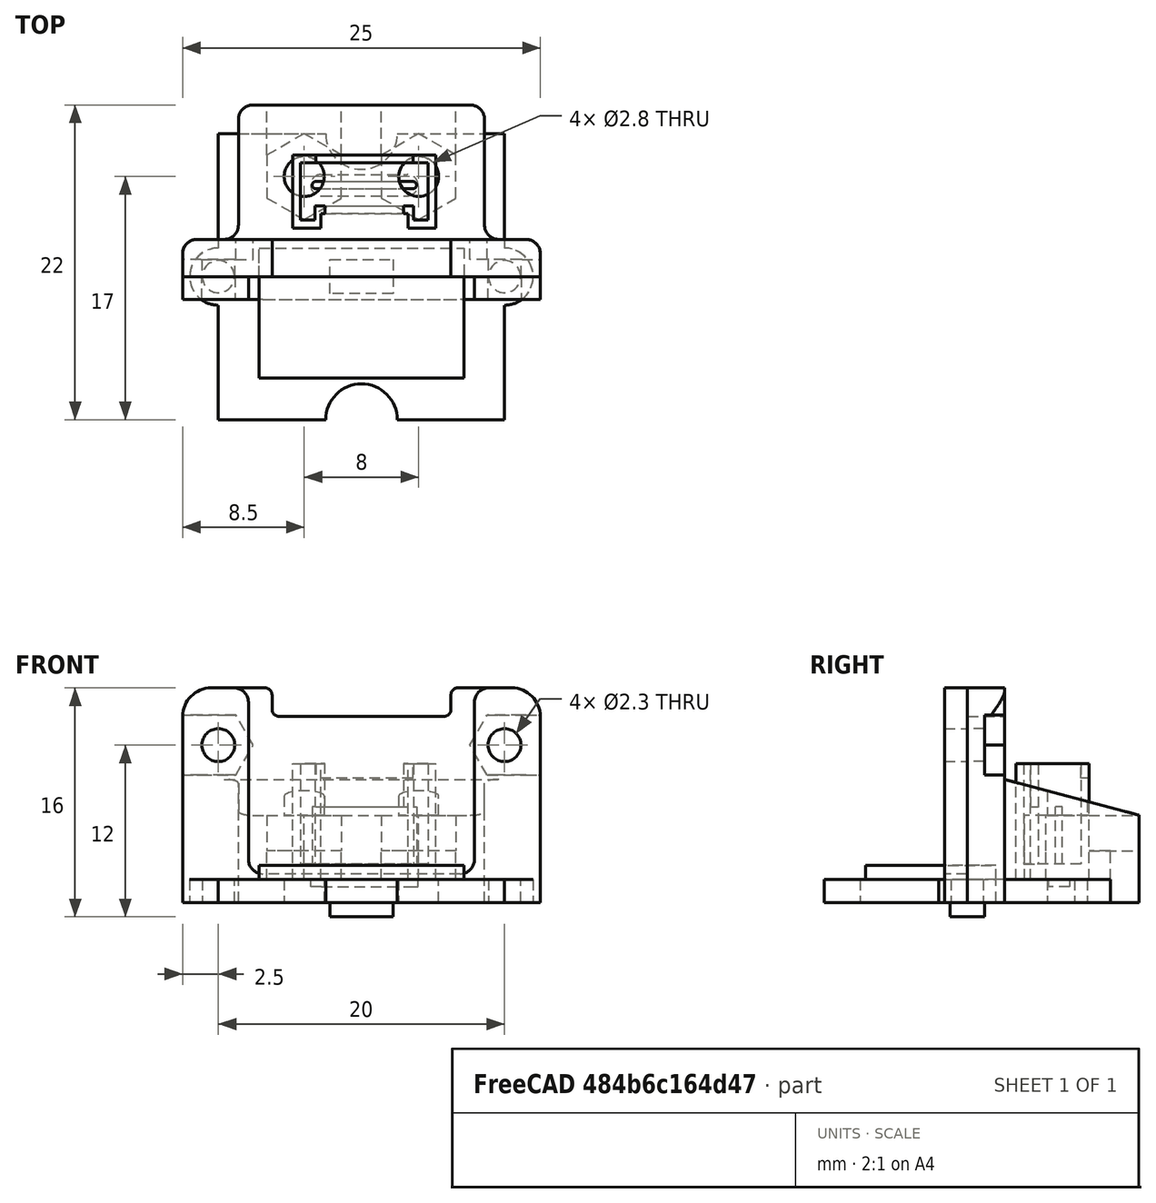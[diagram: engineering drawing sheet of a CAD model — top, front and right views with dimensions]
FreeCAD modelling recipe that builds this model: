
FCSTD DOCUMENT  (FreeCAD 0.19R24276 (Git))
Label: PB3D_TriPlate_LSRMt
License: All rights reserved
LicenseURL: http://en.wikipedia.org/wiki/All_rights_reserved
objects: Sketcher::SketchObject×23, PartDesign::Pocket×13, PartDesign::Pad×8, PartDesign::Body×6, PartDesign::Plane×3, App::Part×2, Mesh::Feature×2, Spreadsheet::Sheet×1
note: 74 computed .brp shape members not serialized (recipe doc carries the construction recipe); baked Part::Feature solids carry a one-line shape summary decoded from their .brp

FEATURE [Spreadsheet::Sheet] Spreadsheet  label="params"
  cells = A1=M2 Bolt Clearances; C1=M2.5 Bolt Clearances; A2=Hole Clear Diam; B2(m2_hole_clear_diam)==2.3mm; C2=Hole Clear Diam; D2(m25_hole_clear_diam)==2.8mm; E2=Std Rad; F2(std_rad)==2mm; A3=Head Clear Diam; B3(m2_head_clear_diam)==4mm; C3=Head Clear Diam; D3(m25_head_clear_diam)==5mm; A4=Head Min Depth; B4(m2_head_min_depth)==1.3mm; C4=Head Min Depth; D4(m25_head_min_depth)==1.6mm; A5=Nut Clear Flat; B5(m2_nut_clear_flat)==4.2mm; C5=Nut Clear Flat; D5(m25_nut_clear_flat)==5.2mm; A6=Nut Min Depth; B6(m2_nut_min_depth)==1.75mm; C6=Nut Min Depth; D6(m25_nut_min_depth)==2mm; A8=LSR Mt; G8=LSR Face Plate; A9=Mt Height; B9(mt_height)==15mm; C9=ToPlate CSunk Z; D9(toplate_csunk_z)==1.6mm; E9=Grove Con Clear Width; F9(grove_clear_width)==12.5mm; G9=Grove Plate Thick; H9(faceplate_grovethick)==1.5mm; A10=Mt Width; B10(mt_width)==25mm; C10=ToPlate CSunk Height; D10(toplate_csunk_height)==m25_nut_min_depth; E10=Grove Con Clear Height; F10(grove_clear_height)==2mm; G10=Grove+Elec thick; H10(faceplate_grovetotthick)==2.75mm; A11=Mt Thick; B11(mt_thick)==2.6mm; C11=ToPlate Slot Z; D11(toplate_slot_z)==toplate_csunk_z + toplate_csunk_height; G11=Face Plate Tol; H11(faceplate_tol)==0.35mm; A12=Foot Width; B12(foot_width)==12mm; C12=ToPlate Slot Height; D12(toplate_slot_height)==m25_nut_min_depth + 0.5mm; G12=Face Plate Thick; H12(faceplate_thick)==faceplate_grovetotthick - faceplate_grovethick + faceplate_tol; A13=Foot Thick; B13(foot_thick)==toplate_slot_z + toplate_slot_height; G13=Face Plate Cut Width; H13(faceplate_cut_width)==15.8mm; C14=ToPlate Hole Spacing Y; D14(toplate_hole_spacing_x)==8mm; G14=Face Plate Bottom Height; H14(faceplate_bottom_height)==2mm; A15=LSR Mt CSunk Offset Z; B15(lsr_mt_csunk_z)==1.2mm; C15=ToPlate Hole Offset X; D15(toplate_hole_offset_y)==5mm; A16=LSR Mt Hole Spacing Width; B16(lsr_mt_hole_spacing_width)==20mm; C16=ToPlate Hole Loc X; D16(toplate_hole_loc_y)==foot_width - toplate_hole_offset_y; A17=LSR Mt Hole Height; B17(lsr_mt_hole_height)==11mm; A19=Sculpt Z Width; B19(sculpt_z_width)==17.2mm
FEATURE [Sketcher::SketchObject] Sketch008
  FullyConstrained = true
  MapMode = 5
  Support = -> [XY_Plane007]
  sketch-geometry (8):
    g0: LineSegment StartX=-5 StartY=0 StartZ=0 EndX=-3.05 EndY=0 EndZ=0
    g1: LineSegment StartX=3.05 StartY=0 StartZ=0 EndX=5 EndY=0 EndZ=0
    g2: LineSegment StartX=-5 StartY=0 StartZ=0 EndX=-5 EndY=5.1 EndZ=0
    g3: LineSegment StartX=-5 StartY=5.1 StartZ=0 EndX=5 EndY=5.1 EndZ=0
    g4: LineSegment StartX=5 StartY=5.1 StartZ=0 EndX=5 EndY=0 EndZ=0
    g5: LineSegment StartX=3.05 StartY=0 StartZ=0 EndX=3.05 EndY=1 EndZ=0
    g6: LineSegment StartX=3.05 StartY=1 StartZ=0 EndX=-3.05 EndY=1 EndZ=0
    g7: LineSegment StartX=-3.05 StartY=1 StartZ=0 EndX=-3.05 EndY=0 EndZ=0
  constraints (23):
    c: PointOnObject(g0,g-1)
    c: PointOnObject(g1,g-1)
    c: PointOnObject(g0,g-1)
    c: Coincident(g2,g0)
    c: Vertical(g2)
    c: Coincident(g3,g2)
    c: Horizontal(g3)
    c: Coincident(g4,g3)
    c: Coincident(g4,g1)
    c: Vertical(g4)
    c: Coincident(g5,g1)
    c: Vertical(g5)
    c: Coincident(g6,g5)
    c: Horizontal(g6)
    c: Coincident(g7,g6)
    c: Coincident(g7,g0)
    c: Vertical(g7)
    c: Equal(g0,g1)
    c: Symmetric(g0,g1,g-1)
    c: Distance(g4) = 5.1
    c: Distance(g6) = 6.1
    c: Distance(g3) = 10
    c: Distance(g7) = 1
FEATURE [PartDesign::Pad] Pad005
  Direction = (1,1,1)
  Length = 8.1
  Length2 = 100
  Profile = -> Sketch008
  Type = 0
FEATURE [Sketcher::SketchObject] Sketch013
  FullyConstrained = true
  MapMode = 5
  Support = -> [XY_Plane007]
  sketch-geometry (5):
    g0: ArcOfCircle CenterX=-3 CenterY=3 CenterZ=0 NormalX=0 NormalY=0 NormalZ=1 AngleXU=0 Radius=0.75 StartAngle=1.5708 EndAngle=4.71239
    g1: ArcOfCircle CenterX=3 CenterY=3 CenterZ=0 NormalX=0 NormalY=0 NormalZ=1 AngleXU=0 Radius=0.75 StartAngle=4.71239 EndAngle=7.85398
    g2: LineSegment StartX=-3 StartY=2.25 StartZ=0 EndX=3 EndY=2.25 EndZ=0
    g3: LineSegment StartX=-3 StartY=3.75 StartZ=0 EndX=3 EndY=3.75 EndZ=0
    g4: LineSegment StartX=0 StartY=0 StartZ=0 EndX=0 EndY=3 EndZ=0
  constraints (12):
    c: Tangent(g0,g3) = 1.5708
    c: Tangent(g0,g2) = -1.5708
    c: Tangent(g2,g1) = -1.5708
    c: Tangent(g3,g1) = 1.5708
    c: Horizontal(g2)
    c: Equal(g0,g1)
    c: Coincident(g4,g-1)
    c: PointOnObject(g4,g-2)
    c: Symmetric(g0,g1,g4)
    c: Distance(g4) = 3
    c: DistanceY(g1,g1) = 1.5
    c: DistanceX(g0,g1) = 6
FEATURE [Sketcher::SketchObject] Sketch009
  FullyConstrained = true
  MapMode = 5
  Placement = pos=(0,0,8.1) rot=(0,0,1;0rad)
  Support = -> [Pad005]
  sketch-geometry (10):
    g0: LineSegment StartX=-4.45 StartY=0.55 StartZ=0 EndX=-3.45 EndY=0.55 EndZ=0
    g1: LineSegment StartX=-3.45 StartY=0.55 StartZ=0 EndX=-3.45 EndY=1.55 EndZ=0
    g2: LineSegment StartX=-3.45 StartY=1.55 StartZ=0 EndX=3.45 EndY=1.55 EndZ=0
    g3: LineSegment StartX=3.45 StartY=1.55 StartZ=0 EndX=3.45 EndY=0.55 EndZ=0
    g4: LineSegment StartX=3.45 StartY=0.55 StartZ=0 EndX=4.45 EndY=0.55 EndZ=0
    g5: LineSegment StartX=4.45 StartY=0.55 StartZ=0 EndX=4.45 EndY=4.55 EndZ=0
    g6: LineSegment StartX=4.45 StartY=4.55 StartZ=0 EndX=-4.45 EndY=4.55 EndZ=0
    g7: LineSegment StartX=-4.45 StartY=4.55 StartZ=0 EndX=-4.45 EndY=0.55 EndZ=0
    g8: LineSegment StartX=-3.45 StartY=0.55 StartZ=0 EndX=3.45 EndY=0.55 EndZ=0
    g9: LineSegment StartX=0 StartY=0 StartZ=0 EndX=0 EndY=0.55 EndZ=0
  constraints (28):
    c: Horizontal(g0)
    c: Coincident(g1,g0)
    c: Coincident(g2,g1)
    c: Horizontal(g2)
    c: Coincident(g3,g2)
    c: Vertical(g3)
    c: Coincident(g4,g3)
    c: Horizontal(g4)
    c: Coincident(g5,g4)
    c: Vertical(g5)
    c: Coincident(g6,g5)
    c: Horizontal(g6)
    c: Coincident(g7,g6)
    c: Coincident(g7,g0)
    c: Vertical(g7)
    c: Vertical(g1)
    c: Coincident(g8,g0)
    c: Coincident(g8,g3)
    c: Horizontal(g8)
    c: Equal(g0,g4)
    c: Coincident(g9,g-1)
    c: PointOnObject(g9,g-2)
    c: Symmetric(g0,g3,g9)
    c: Distance(g0) = 1
    c: Distance(g1) = 1
    c: Distance(g9) = 0.55
    c: Distance(g6) = 8.9
    c: DistanceY(g2,g5) = 3
FEATURE [PartDesign::Pocket] Pocket003
  BaseFeature = -> Pad005
  Length = 7
  Length2 = 100
  Profile = -> Sketch009
  Type = 0
FEATURE [Sketcher::SketchObject] Sketch010
  FullyConstrained = true
  MapMode = 5
  Placement = pos=(0,0,8.1) rot=(0,0,1;0rad)
  Support = -> [Pocket003]
  sketch-geometry (5):
    g0: LineSegment StartX=0 StartY=0 StartZ=0 EndX=0 EndY=3 EndZ=0
    g1: LineSegment StartX=-3.4 StartY=8 StartZ=0 EndX=3.4 EndY=8 EndZ=0
    g2: LineSegment StartX=3.4 StartY=8 StartZ=0 EndX=3.4 EndY=3 EndZ=0
    g3: LineSegment StartX=3.4 StartY=3 StartZ=0 EndX=-3.4 EndY=3 EndZ=0
    g4: LineSegment StartX=-3.4 StartY=3 StartZ=0 EndX=-3.4 EndY=8 EndZ=0
  constraints (14):
    c: Coincident(g0,g-1)
    c: PointOnObject(g0,g-2)
    c: Coincident(g1,g2)
    c: Coincident(g2,g3)
    c: Coincident(g3,g4)
    c: Coincident(g4,g1)
    c: Horizontal(g1)
    c: Horizontal(g3)
    c: Vertical(g2)
    c: Vertical(g4)
    c: Symmetric(g3,g2,g0)
    c: Distance(g0) = 3
    c: Distance(g2) = 5
    c: Distance(g1) = 6.8
FEATURE [PartDesign::Pocket] Pocket004
  BaseFeature = -> Pocket003
  Length = 1
  Length2 = 100
  Profile = -> Sketch010
  Type = 0
FEATURE [Sketcher::SketchObject] Sketch011
  FullyConstrained = true
  MapMode = 5
  Placement = pos=(0,0,8.1) rot=(0,0,1;0rad)
  Support = -> [Pocket004]
  sketch-geometry (4):
    g0: LineSegment StartX=-2.75 StartY=3 StartZ=0 EndX=2.75 EndY=3 EndZ=0
    g1: LineSegment StartX=2.75 StartY=3 StartZ=0 EndX=2.75 EndY=0 EndZ=0
    g2: LineSegment StartX=2.75 StartY=0 StartZ=0 EndX=-2.75 EndY=0 EndZ=0
    g3: LineSegment StartX=-2.75 StartY=0 StartZ=0 EndX=-2.75 EndY=3 EndZ=0
  constraints (11):
    c: Coincident(g0,g1)
    c: Coincident(g1,g2)
    c: Coincident(g2,g3)
    c: Coincident(g3,g0)
    c: Horizontal(g0)
    c: Horizontal(g2)
    c: Vertical(g1)
    c: Vertical(g3)
    c: Symmetric(g2,g1,g-1)
    c: Distance(g1) = 3
    c: Distance(g0) = 5.5
FEATURE [PartDesign::Pocket] Pocket005
  BaseFeature = -> Pocket004
  Length = 3
  Length2 = 100
  Profile = -> Sketch011
  Type = 0
FEATURE [Sketcher::SketchObject] Sketch015
  FullyConstrained = true
  MapMode = 5
  Support = -> [XY_Plane010]
  sketch-geometry (4):
    g0: LineSegment StartX=-7.15 StartY=0 StartZ=0 EndX=7.15 EndY=0 EndZ=0
    g1: LineSegment StartX=7.15 StartY=0 StartZ=0 EndX=7.15 EndY=-9.1 EndZ=0
    g2: LineSegment StartX=7.15 StartY=-9.1 StartZ=0 EndX=-7.15 EndY=-9.1 EndZ=0
    g3: LineSegment StartX=-7.15 StartY=-9.1 StartZ=0 EndX=-7.15 EndY=0 EndZ=0
  constraints (11):
    c: Coincident(g0,g1)
    c: Coincident(g1,g2)
    c: Coincident(g2,g3)
    c: Coincident(g3,g0)
    c: Horizontal(g0)
    c: Horizontal(g2)
    c: Vertical(g1)
    c: Vertical(g3)
    c: Symmetric(g0,g0,g-1)
    c: Distance(g0) = 14.3
    c: Distance(g1) = 9.1
FEATURE [PartDesign::Pad] Pad009
  Direction = (1,1,1)
  Length = 1
  Length2 = 100
  Profile = -> Sketch015
  Type = 0
FEATURE [Sketcher::SketchObject] Sketch014
  FullyConstrained = true
  MapMode = 5
  Support = -> [XY_Plane010]
  sketch-geometry (6):
    g0: LineSegment StartX=-2.2 StartY=1.2 StartZ=0 EndX=2.2 EndY=1.2 EndZ=0
    g1: LineSegment StartX=2.2 StartY=1.2 StartZ=0 EndX=2.2 EndY=-1.2 EndZ=0
    g2: LineSegment StartX=2.2 StartY=-1.2 StartZ=0 EndX=-2.2 EndY=-1.2 EndZ=0
    g3: LineSegment StartX=-2.2 StartY=-1.2 StartZ=0 EndX=-2.2 EndY=1.2 EndZ=0
    g4: LineSegment StartX=0 StartY=0 StartZ=0 EndX=0 EndY=1.2 EndZ=0
    g5: LineSegment StartX=0 StartY=0 StartZ=0 EndX=2.2 EndY=0 EndZ=0
  constraints (16):
    c: Coincident(g0,g1)
    c: Coincident(g1,g2)
    c: Coincident(g2,g3)
    c: Coincident(g3,g0)
    c: Horizontal(g0)
    c: Horizontal(g2)
    c: Vertical(g1)
    c: Vertical(g3)
    c: Coincident(g4,g-1)
    c: PointOnObject(g4,g-2)
    c: Coincident(g5,g-1)
    c: PointOnObject(g5,g-1)
    c: Symmetric(g0,g0,g4)
    c: Symmetric(g0,g1,g5)
    c: Distance(g0) = 4.4
    c: Distance(g1) = 2.4
FEATURE [PartDesign::Pad] Pad008
  Direction = (1,1,1)
  Length = 1
  Length2 = 100
  Profile = -> Sketch014
  Reversed = true
  Type = 0
FEATURE [Sketcher::SketchObject] Sketch
  FullyConstrained = true
  MapMode = 5
  Support = -> [XY_Plane011]
  sketch-geometry (16):
    g0: LineSegment StartX=-10 StartY=10 StartZ=0 EndX=-2.5 EndY=10 EndZ=0
    g1: LineSegment StartX=2.5 StartY=10 StartZ=0 EndX=10 EndY=10 EndZ=0
    g2: LineSegment StartX=10 StartY=10 StartZ=0 EndX=10 EndY=2 EndZ=0
    g3: LineSegment StartX=10 StartY=-2 StartZ=0 EndX=10 EndY=-10 EndZ=0
    g4: LineSegment StartX=10 StartY=-10 StartZ=0 EndX=2.5 EndY=-10 EndZ=0
    g5: LineSegment StartX=-2.5 StartY=-10 StartZ=0 EndX=-10 EndY=-10 EndZ=0
    g6: LineSegment StartX=-10 StartY=-10 StartZ=0 EndX=-10 EndY=-2 EndZ=0
    g7: LineSegment StartX=-10 StartY=10 StartZ=0 EndX=-10 EndY=2 EndZ=0
    g8: ArcOfCircle CenterX=0 CenterY=10 CenterZ=0 NormalX=0 NormalY=0 NormalZ=1 AngleXU=0 Radius=2.5 StartAngle=3.14159 EndAngle=6.28319
    g9: ArcOfCircle CenterX=0 CenterY=-10 CenterZ=0 NormalX=0 NormalY=0 NormalZ=1 AngleXU=0 Radius=2.5 StartAngle=0 EndAngle=3.14159
    g10: LineSegment StartX=-2.5 StartY=10 StartZ=0 EndX=2.5 EndY=10 EndZ=0
    g11: LineSegment StartX=-2.5 StartY=-10 StartZ=0 EndX=2.5 EndY=-10 EndZ=0
    g12: LineSegment StartX=-10 StartY=2 StartZ=0 EndX=-10 EndY=-2 EndZ=0
    g13: LineSegment StartX=10 StartY=2 StartZ=0 EndX=10 EndY=-2 EndZ=0
    g14: ArcOfCircle CenterX=-10 CenterY=0 CenterZ=0 NormalX=0 NormalY=0 NormalZ=1 AngleXU=0 Radius=2 StartAngle=1.5708 EndAngle=4.71239
    g15: ArcOfCircle CenterX=10 CenterY=0 CenterZ=0 NormalX=0 NormalY=0 NormalZ=1 AngleXU=0 Radius=2 StartAngle=4.71239 EndAngle=7.85398
  constraints (48):
    c: Horizontal(g0)
    c: Horizontal(g1)
    c: Coincident(g2,g1)
    c: Vertical(g2)
    c: Vertical(g3)
    c: Coincident(g4,g3)
    c: Horizontal(g4)
    c: Horizontal(g5)
    c: Coincident(g6,g5)
    c: Vertical(g6)
    c: Coincident(g7,g0)
    c: Vertical(g7)
    c: PointOnObject(g8,g-2)
    c: Coincident(g8,g0)
    c: Coincident(g8,g1)
    c: PointOnObject(g9,g-2)
    c: Coincident(g9,g5)
    c: Coincident(g9,g4)
    c: Coincident(g10,g0)
    c: Coincident(g10,g1)
    c: Coincident(g11,g5)
    c: Coincident(g11,g4)
    c: Horizontal(g11)
    c: PointOnObject(g9,g11)
    c: PointOnObject(g8,g10)
    c: Horizontal(g10)
    c: Coincident(g12,g7)
    c: Coincident(g12,g6)
    c: Coincident(g13,g2)
    c: Coincident(g13,g3)
    c: Equal(g10,g11)
    c: Equal(g13,g12)
    c: Vertical(g12)
    c: Vertical(g13)
    c: PointOnObject(g14,g-1)
    c: Coincident(g14,g7)
    c: Coincident(g14,g6)
    c: PointOnObject(g15,g-1)
    c: Coincident(g15,g2)
    c: Coincident(g15,g3)
    c: PointOnObject(g14,g12)
    c: PointOnObject(g15,g13)
    c: Equal(g7,g6)
    c: Equal(g1,g0)
    c: Diameter(g14) = 4
    c: Diameter(g8) = 5
    c: DistanceY(g3,g1) = 20
    c: DistanceX(g0,g1) = 20
FEATURE [PartDesign::Pad] Pad
  Direction = (1,1,1)
  Length = 1.6
  Length2 = 100
  Profile = -> Sketch
  Type = 0
FEATURE [Sketcher::SketchObject] Sketch001
  FullyConstrained = true
  MapMode = 5
  Support = -> [XY_Plane011]
  sketch-geometry (2):
    g0: Circle CenterX=-10 CenterY=0 CenterZ=0 NormalX=0 NormalY=0 NormalZ=1 AngleXU=0 Radius=1.125
    g1: Circle CenterX=10 CenterY=0 CenterZ=0 NormalX=0 NormalY=0 NormalZ=1 AngleXU=0 Radius=1.125
  constraints (5):
    c: PointOnObject(g1,g-1)
    c: Symmetric(g0,g1,g-1)
    c: Equal(g0,g1)
    c: Diameter(g0) = 2.25
    c: DistanceX(g0,g1) = 20
FEATURE [PartDesign::Pocket] Pocket
  BaseFeature = -> Pad
  Length = 5
  Length2 = 100
  Profile = -> Sketch001
  Reversed = true
  Type = 1
FEATURE [Sketcher::SketchObject] Sketch012
  FullyConstrained = true
  MapMode = 5
  Placement = pos=(0,0,1.1) rot=(0,0,1;0rad)
  Support = -> [Pocket005]
  sketch-geometry (5):
    g0: ArcOfCircle CenterX=-3.4 CenterY=3 CenterZ=0 NormalX=0 NormalY=0 NormalZ=1 AngleXU=0 Radius=0.25 StartAngle=1.5708 EndAngle=4.71239
    g1: ArcOfCircle CenterX=3.4 CenterY=3 CenterZ=0 NormalX=0 NormalY=0 NormalZ=1 AngleXU=0 Radius=0.25 StartAngle=4.71239 EndAngle=7.85398
    g2: LineSegment StartX=-3.4 StartY=2.75 StartZ=0 EndX=3.4 EndY=2.75 EndZ=0
    g3: LineSegment StartX=-3.4 StartY=3.25 StartZ=0 EndX=3.4 EndY=3.25 EndZ=0
    g4: LineSegment StartX=0 StartY=0 StartZ=0 EndX=0 EndY=2.75 EndZ=0
  constraints (12):
    c: Tangent(g0,g3) = 1.5708
    c: Tangent(g0,g2) = -1.5708
    c: Tangent(g2,g1) = -1.5708
    c: Tangent(g3,g1) = 1.5708
    c: Horizontal(g2)
    c: Equal(g0,g1)
    c: Coincident(g4,g-1)
    c: PointOnObject(g4,g-2)
    c: Symmetric(g0,g1,g4)
    c: DistanceY(g-1,g1) = 3
    c: DistanceY(g1,g1) = 0.5
    c: DistanceX(g0,g1) = 6.8
FEATURE [PartDesign::Pad] Pad006
  BaseFeature = -> Pocket005
  Direction = (1,1,1)
  Length = 4
  Length2 = 100
  Profile = -> Sketch012
  Type = 0
FEATURE [PartDesign::Pad] Pad007
  BaseFeature = -> Pad006
  Direction = (1,1,1)
  Length = 0.5
  Length2 = 100
  Profile = -> Sketch013
  Reversed = true
  Type = 0
FEATURE [PartDesign::Body] Body001  label="GroveBoard"
  Group = -> [Sketch,Pad,Sketch001,Pocket]
  Origin = -> Origin003
  Tip = -> Pocket
FEATURE [PartDesign::Body] Body005  label="GroveHeader1"
  Group = -> [Sketch008,Pad005,Sketch009,Pocket003,Sketch010,Pocket004,Sketch011,Pocket005,Sketch012,Pad006,Sketch013,Pad007]
  Origin = -> Origin007
  Placement = pos=(0.2,3.4,1.6) rot=(0,0,1;0rad)
  Tip = -> Pad007
FEATURE [PartDesign::Body] Body006  label="LaserDistSens"
  Group = -> [Sketch014,Pad008]
  Origin = -> Origin008
  Tip = -> Pad008
FEATURE [PartDesign::Body] Body007  label="MiscElectronics"
  Group = -> [Sketch015,Pad009]
  Origin = -> Origin009
  Placement = pos=(0,2,1.6) rot=(0,0,1;0rad)
  Tip = -> Pad009
FEATURE [App::Part] Part001  label="Grove_LSR"
  Group = -> [Body001,Body005,Body006,Body007]
  Origin = -> Origin002
  Placement = pos=(-4e-16,-3,11) rot=(0,0.707107,0.707107;3.14159rad)
FEATURE [Sketcher::SketchObject] Sketch016  label="Sketch_MainMtExt"
  FullyConstrained = true
  MapMode = 5
  Placement = pos=(0,0,0) rot=(0.57735,0.57735,0.57735;2.0944rad)
  Support = -> [YZ_Plane001]
  expr: Constraints[11] = <<params>>.foot_thick
  expr: Constraints[8] = <<params>>.foot_width
  expr: Constraints[10] = <<params>>.mt_height
  expr: Constraints[9] = <<params>>.mt_thick
  sketch-geometry (6):
    g0: LineSegment StartX=0 StartY=0 StartZ=0 EndX=0 EndY=15 EndZ=0
    g1: LineSegment StartX=0 StartY=0 StartZ=0 EndX=12 EndY=0 EndZ=0
    g2: LineSegment StartX=0 StartY=15 StartZ=0 EndX=2.6 EndY=15 EndZ=0
    g3: LineSegment StartX=12 StartY=0 StartZ=0 EndX=12 EndY=6.1 EndZ=0
    g4: LineSegment StartX=2.6 StartY=15 StartZ=0 EndX=2.6 EndY=8.6 EndZ=0
    g5: LineSegment StartX=12 StartY=6.1 StartZ=0 EndX=2.6 EndY=8.6 EndZ=0
  constraints (17):
    c: Coincident(g0,g-1)
    c: PointOnObject(g0,g-2)
    c: Coincident(g1,g0)
    c: PointOnObject(g1,g-1)
    c: Coincident(g2,g0)
    c: Horizontal(g2)
    c: Coincident(g3,g1)
    c: Vertical(g3)
    c: DistanceX(g0,g1) = 12
    c: DistanceX(g0,g2) = 2.6
    c: DistanceY(g0,g0) = 15
    c: DistanceY(g1,g3) = 6.1
    c: Coincident(g4,g2)
    c: Vertical(g4)
    c: Coincident(g5,g3)
    c: Coincident(g5,g4)
    c: DistanceY(g3,g4) = 2.5
FEATURE [PartDesign::Pad] Pad010  label="MainExt"
  Direction = (1,1,1)
  Length = 25
  Length2 = 100
  Midplane = true
  Placement = pos=(0,0,0) rot=(0.57735,0.57735,0.57735;2.0944rad)
  Profile = -> Sketch016
  Type = 0
FEATURE [PartDesign::Plane] DatumPlane  label="Datum_ToPlateCSunkZ"
  AttachmentOffset = pos=(0,0,1.6) rot=(0,0,1;0rad)
  Length = 60
  MapMode = 5
  Placement = pos=(0,0,1.6) rot=(0,0,1;0rad)
  ResizeMode = 0
  Support = -> [XY_Plane001]
  Width = 60
  expr: .AttachmentOffset.Base.z = <<params>>.toplate_csunk_z
FEATURE [PartDesign::Plane] DatumPlane001  label="Datum_ToPlateSlotZ"
  AttachmentOffset = pos=(0,0,3.6) rot=(0,0,1;0rad)
  Length = 60
  MapMode = 5
  Placement = pos=(0,0,3.6) rot=(0,0,1;0rad)
  ResizeMode = 0
  Support = -> [XY_Plane001]
  Width = 60
  expr: .AttachmentOffset.Base.z = <<params>>.toplate_slot_z
FEATURE [Sketcher::SketchObject] Sketch017  label="Sketch_ToPlate_Temp"
  FullyConstrained = true
  MapMode = 5
  Support = -> [XY_Plane001]
  expr: Constraints[5] = Spreadsheet.toplate_hole_loc_y
  expr: Constraints[4] = Spreadsheet.toplate_hole_spacing_x
  sketch-geometry (2):
    g0: LineSegment StartX=0 StartY=0 StartZ=0 EndX=0 EndY=7 EndZ=0
    g1: LineSegment StartX=-4 StartY=7 StartZ=0 EndX=4 EndY=7 EndZ=0
  constraints (6):
    c: Coincident(g0,g-1)
    c: PointOnObject(g0,g-2)
    c: Horizontal(g1)
    c: Symmetric(g1,g1,g0)
    c: DistanceX(g1,g1) = 8
    c: DistanceY(g-1,g0) = 7
FEATURE [Sketcher::SketchObject] Sketch018  label="Sketch_ToPlate_Holes"
  FullyConstrained = true
  MapMode = 5
  Support = -> [XY_Plane001]
  expr: Constraints[9] = <<params>>.m25_hole_clear_diam
  expr: Constraints[4] = Spreadsheet.toplate_hole_spacing_x
  expr: Constraints[5] = Spreadsheet.toplate_hole_loc_y
  sketch-geometry (4):
    g0: LineSegment StartX=0 StartY=0 StartZ=0 EndX=0 EndY=7 EndZ=0
    g1: LineSegment StartX=-4 StartY=7 StartZ=0 EndX=4 EndY=7 EndZ=0
    g2: Circle CenterX=-4 CenterY=7 CenterZ=0 NormalX=0 NormalY=0 NormalZ=1 AngleXU=0 Radius=1.4
    g3: Circle CenterX=4 CenterY=7 CenterZ=0 NormalX=0 NormalY=0 NormalZ=1 AngleXU=0 Radius=1.4
  constraints (10):
    c: Coincident(g0,g-1)
    c: PointOnObject(g0,g-2)
    c: Horizontal(g1)
    c: Symmetric(g1,g1,g0)
    c: DistanceX(g1,g1) = 8
    c: DistanceY(g-1,g0) = 7
    c: Coincident(g2,g1)
    c: Coincident(g3,g1)
    c: Equal(g3,g2)
    c: Diameter(g3) = 2.8
FEATURE [PartDesign::Pocket] Pocket006  label="ToPlateMtHoles"
  BaseFeature = -> Pad010
  Length = 5
  Length2 = 100
  Placement = pos=(0,0,0) rot=(0.57735,0.57735,0.57735;2.0944rad)
  Profile = -> Sketch018
  Reversed = true
  Type = 1
FEATURE [Sketcher::SketchObject] Sketch019  label="Sketch_ToPlate_CSunk"
  FullyConstrained = true
  MapMode = 5
  Placement = pos=(0,0,1.6) rot=(0,0,1;0rad)
  Support = -> [DatumPlane]
  expr: Constraints[45] = <<params>>.m25_nut_clear_flat
  expr: Constraints[4] = Spreadsheet.toplate_hole_spacing_x
  expr: Constraints[5] = Spreadsheet.toplate_hole_loc_y
  sketch-geometry (16):
    g0: LineSegment StartX=0 StartY=0 StartZ=0 EndX=0 EndY=7 EndZ=0
    g1: LineSegment StartX=-4 StartY=7 StartZ=0 EndX=4 EndY=7 EndZ=0
    g2: LineSegment StartX=-4 StartY=10.0022 StartZ=0 EndX=-6.6 EndY=8.50111 EndZ=0
    g3: LineSegment StartX=-6.6 StartY=8.50111 StartZ=0 EndX=-6.6 EndY=5.49889 EndZ=0
    g4: LineSegment StartX=-6.6 StartY=5.49889 StartZ=0 EndX=-4 EndY=3.99778 EndZ=0
    g5: LineSegment StartX=-4 StartY=3.99778 StartZ=0 EndX=-1.4 EndY=5.49889 EndZ=0
    g6: LineSegment StartX=-1.4 StartY=5.49889 StartZ=0 EndX=-1.4 EndY=8.50111 EndZ=0
    g7: LineSegment StartX=-1.4 StartY=8.50111 StartZ=0 EndX=-4 EndY=10.0022 EndZ=0
    g8: Circle CenterX=-4 CenterY=7 CenterZ=0 NormalX=0 NormalY=0 NormalZ=1 AngleXU=0 Radius=3.00222
    g9: LineSegment StartX=4 StartY=10.0022 StartZ=0 EndX=1.4 EndY=8.50111 EndZ=0
    g10: LineSegment StartX=1.4 StartY=8.50111 StartZ=0 EndX=1.4 EndY=5.49889 EndZ=0
    g11: LineSegment StartX=1.4 StartY=5.49889 StartZ=0 EndX=4 EndY=3.99778 EndZ=0
    g12: LineSegment StartX=4 StartY=3.99778 StartZ=0 EndX=6.6 EndY=5.49889 EndZ=0
    g13: LineSegment StartX=6.6 StartY=5.49889 StartZ=0 EndX=6.6 EndY=8.50111 EndZ=0
    g14: LineSegment StartX=6.6 StartY=8.50111 StartZ=0 EndX=4 EndY=10.0022 EndZ=0
    g15: Circle CenterX=4 CenterY=7 CenterZ=0 NormalX=0 NormalY=0 NormalZ=1 AngleXU=0 Radius=3.00222
  constraints (38):
    c: Coincident(g0,g-1)
    c: PointOnObject(g0,g-2)
    c: Horizontal(g1)
    c: Symmetric(g1,g1,g0)
    c: DistanceX(g1,g1) = 8
    c: DistanceY(g-1,g0) = 7
    c: Coincident(g2,g3)
    c: Coincident(g3,g4)
    c: Coincident(g4,g5)
    c: Coincident(g5,g6)
    c: Coincident(g6,g7)
    c: Coincident(g7,g2)
    c: Equal(g2, g3-g7) x5
    c: PointOnObject(g2,g8)
    c: PointOnObject(g3,g8)
    c: PointOnObject(g4,g8)
    c: PointOnObject(g5,g8)
    c: PointOnObject(g6,g8)
    c: PointOnObject(g7,g8)
    c: Coincident(g8,g1)
    c: Coincident(g9,g10)
    c: Coincident(g10,g11)
    c: Coincident(g11,g12)
    c: Coincident(g12,g13)
    c: Coincident(g13,g14)
    c: Coincident(g14,g9)
    c: Equal(g9, g10-g14) x5
    c: PointOnObject(g9,g15)
    c: PointOnObject(g10,g15)
    c: PointOnObject(g11,g15)
    c: PointOnObject(g12,g15)
    c: PointOnObject(g13,g15)
    c: PointOnObject(g14,g15)
    c: Coincident(g15,g1)
    c: Vertical(g10)
    c: Vertical(g6)
    c: Equal(g8,g15)
    c: DistanceX(g10,g12) = 5.2
FEATURE [PartDesign::Pocket] Pocket007  label="ToPlateCSunk"
  BaseFeature = -> Pocket006
  Length = 2
  Length2 = 100
  Placement = pos=(0,0,0) rot=(0.57735,0.57735,0.57735;2.0944rad)
  Profile = -> Sketch019
  Reversed = true
  Type = 0
  expr: Length = <<params>>.m25_nut_min_depth
FEATURE [Sketcher::SketchObject] Sketch020  label="Sketch_ToPlate_Temp001"
  FullyConstrained = true
  MapMode = 5
  Placement = pos=(0,0,3.6) rot=(0,0,1;0rad)
  Support = -> [DatumPlane001]
  expr: Constraints[50] = <<params>>.foot_width
  expr: Constraints[35] = <<params>>.m25_nut_clear_flat
  expr: Constraints[4] = Spreadsheet.toplate_hole_spacing_x
  expr: Constraints[5] = Spreadsheet.toplate_hole_loc_y
  sketch-geometry (18):
    g0: LineSegment StartX=0 StartY=0 StartZ=0 EndX=0 EndY=7 EndZ=0
    g1: LineSegment StartX=-4 StartY=7 StartZ=0 EndX=4 EndY=7 EndZ=0
    g2: LineSegment StartX=-4 StartY=3.99778 StartZ=0 EndX=-1.4 EndY=5.49889 EndZ=0
    g3: LineSegment StartX=-1.4 StartY=5.49889 StartZ=0 EndX=-1.4 EndY=8.50111 EndZ=0
    g4: LineSegment StartX=-6.6 StartY=8.50111 StartZ=0 EndX=-6.6 EndY=5.49889 EndZ=0
    g5: LineSegment StartX=-6.6 StartY=5.49889 StartZ=0 EndX=-4 EndY=3.99778 EndZ=0
    g6: Circle CenterX=-4 CenterY=7 CenterZ=0 NormalX=0 NormalY=0 NormalZ=1 AngleXU=0 Radius=3.00222
    g7: LineSegment StartX=4 StartY=3.99778 StartZ=0 EndX=6.6 EndY=5.49889 EndZ=0
    g8: LineSegment StartX=6.6 StartY=5.49889 StartZ=0 EndX=6.6 EndY=8.50111 EndZ=0
    g9: LineSegment StartX=1.4 StartY=8.50111 StartZ=0 EndX=1.4 EndY=5.49889 EndZ=0
    g10: LineSegment StartX=1.4 StartY=5.49889 StartZ=0 EndX=4 EndY=3.99778 EndZ=0
    g11: Circle CenterX=4 CenterY=7 CenterZ=0 NormalX=0 NormalY=0 NormalZ=1 AngleXU=0 Radius=3.00222
    g12: LineSegment StartX=-6.6 StartY=8.50111 StartZ=0 EndX=-6.6 EndY=20.5011 EndZ=0
    g13: LineSegment StartX=-1.4 StartY=8.50111 StartZ=0 EndX=-1.4 EndY=20.5011 EndZ=0
    g14: LineSegment StartX=1.4 StartY=8.50111 StartZ=0 EndX=1.4 EndY=20.5011 EndZ=0
    g15: LineSegment StartX=6.6 StartY=8.50111 StartZ=0 EndX=6.6 EndY=20.5011 EndZ=0
    g16: LineSegment StartX=1.4 StartY=20.5011 StartZ=0 EndX=6.6 EndY=20.5011 EndZ=0
    g17: LineSegment StartX=-1.4 StartY=20.5011 StartZ=0 EndX=-6.6 EndY=20.5011 EndZ=0
  constraints (52):
    c: Coincident(g0,g-1)
    c: PointOnObject(g0,g-2)
    c: Horizontal(g1)
    c: Symmetric(g1,g1,g0)
    c: DistanceX(g1,g1) = 8
    c: DistanceY(g-1,g0) = 7
    c: Coincident(g2,g3)
    c: Coincident(g4,g5)
    c: Coincident(g5,g2)
    c: Equal(g2,g3)
    c: Equal(g2,g4)
    c: Equal(g2,g5)
    c: PointOnObject(g2,g6)
    c: PointOnObject(g3,g6)
    c: PointOnObject(g4,g6)
    c: PointOnObject(g4,g6)
    c: PointOnObject(g5,g6)
    c: Coincident(g6,g1)
    c: Coincident(g7,g8)
    c: Coincident(g9,g10)
    c: Coincident(g10,g7)
    c: Equal(g7,g8)
    c: Equal(g7,g9)
    c: Equal(g7,g10)
    c: PointOnObject(g7,g11)
    c: PointOnObject(g8,g11)
    c: PointOnObject(g9,g11)
    c: PointOnObject(g9,g11)
    c: PointOnObject(g10,g11)
    c: Coincident(g11,g1)
    c: Vertical(g4)
    c: Vertical(g8)
    c: Equal(g6,g11)
    c: Vertical(g3)
    c: Vertical(g9)
    c: DistanceX(g9,g7) = 5.2
    c: Coincident(g12,g4)
    c: Vertical(g12)
    c: Coincident(g13,g3)
    c: Vertical(g13)
    c: Coincident(g14,g9)
    c: Vertical(g14)
    c: Coincident(g15,g8)
    c: Vertical(g15)
    c: Coincident(g16,g14)
    c: Coincident(g16,g15)
    c: Horizontal(g16)
    c: Coincident(g17,g13)
    c: Coincident(g17,g12)
    c: Horizontal(g17)
    c: Distance(g15) = 12
    c: Equal(g14,g13)
FEATURE [PartDesign::Pocket] Pocket008  label="ToPlateSlot"
  BaseFeature = -> Pocket007
  Length = 2.5
  Length2 = 100
  Placement = pos=(0,0,0) rot=(0.57735,0.57735,0.57735;2.0944rad)
  Profile = -> Sketch020
  Reversed = true
  Type = 0
  expr: Length = <<params>>.toplate_slot_height
FEATURE [Sketcher::SketchObject] Sketch021  label="Sketch_SculptAlongZ"
  FullyConstrained = true
  MapMode = 5
  Support = -> [XY_Plane001]
  expr: Constraints[31] = <<params>>.sculpt_z_width
  expr: Constraints[30] = <<params>>.mt_width
  expr: Constraints[26] = <<params>>.mt_thick
  expr: Constraints[29] = <<params>>.foot_width
  sketch-geometry (18):
    g0: LineSegment StartX=-12.5 StartY=0 StartZ=0 EndX=-12.5 EndY=1.6 EndZ=0
    g1: LineSegment StartX=-11.5 StartY=2.6 StartZ=0 EndX=-9.6 EndY=2.6 EndZ=0
    g2: LineSegment StartX=-8.6 StartY=3.6 StartZ=0 EndX=-8.6 EndY=11 EndZ=0
    g3: LineSegment StartX=-7.6 StartY=12 StartZ=0 EndX=7.6 EndY=12 EndZ=0
    g4: LineSegment StartX=8.6 StartY=11 StartZ=0 EndX=8.6 EndY=3.6 EndZ=0
    g5: LineSegment StartX=9.6 StartY=2.6 StartZ=0 EndX=11.5 EndY=2.6 EndZ=0
    g6: LineSegment StartX=12.5 StartY=1.6 StartZ=0 EndX=12.5 EndY=0 EndZ=0
    g7: ArcOfCircle CenterX=-11.5 CenterY=1.6 CenterZ=0 NormalX=0 NormalY=0 NormalZ=1 AngleXU=0 Radius=1 StartAngle=1.5708 EndAngle=3.14159
    g8: ArcOfCircle CenterX=-9.6 CenterY=3.6 CenterZ=0 NormalX=0 NormalY=0 NormalZ=1 AngleXU=0 Radius=1 StartAngle=4.71239 EndAngle=6.28319
    g9: ArcOfCircle CenterX=-7.6 CenterY=11 CenterZ=0 NormalX=0 NormalY=0 NormalZ=1 AngleXU=0 Radius=1 StartAngle=1.5708 EndAngle=3.14159
    g10: ArcOfCircle CenterX=7.6 CenterY=11 CenterZ=0 NormalX=0 NormalY=0 NormalZ=1 AngleXU=0 Radius=1 StartAngle=0 EndAngle=1.5708
    g11: ArcOfCircle CenterX=9.6 CenterY=3.6 CenterZ=0 NormalX=0 NormalY=0 NormalZ=1 AngleXU=0 Radius=1 StartAngle=3.14159 EndAngle=4.71239
    g12: ArcOfCircle CenterX=11.5 CenterY=1.6 CenterZ=0 NormalX=0 NormalY=0 NormalZ=1 AngleXU=0 Radius=1 StartAngle=0 EndAngle=1.5708
    g13: LineSegment StartX=-12.5 StartY=0 StartZ=0 EndX=-22.5 EndY=0 EndZ=0
    g14: LineSegment StartX=12.5 StartY=0 StartZ=0 EndX=22.5 EndY=0 EndZ=0
    g15: LineSegment StartX=22.5 StartY=0 StartZ=0 EndX=22.5 EndY=22 EndZ=0
    g16: LineSegment StartX=22.5 StartY=22 StartZ=0 EndX=-22.5 EndY=22 EndZ=0
    g17: LineSegment StartX=-22.5 StartY=22 StartZ=0 EndX=-22.5 EndY=0 EndZ=0
  constraints (47):
    c: Symmetric(g0,g6,g-1)
    c: Vertical(g0)
    c: Horizontal(g1)
    c: Vertical(g2)
    c: Horizontal(g3)
    c: Vertical(g4)
    c: Horizontal(g5)
    c: Vertical(g6)
    c: Equal(g5,g1)
    c: Tangent(g0,g7) = 1.5708
    c: Tangent(g1,g7) = 1.5708
    c: Tangent(g1,g8) = -1.5708
    c: Tangent(g2,g8) = -1.5708
    c: Tangent(g2,g9) = 1.5708
    c: Tangent(g3,g9) = 1.5708
    c: Tangent(g3,g10) = 1.5708
    c: Tangent(g4,g10) = 1.5708
    c: Tangent(g4,g11) = -1.5708
    c: Tangent(g5,g11) = -1.5708
    c: Tangent(g5,g12) = 1.5708
    c: Tangent(g6,g12) = 1.5708
    c: Equal(g10,g9)
    c: Equal(g8,g11)
    c: Equal(g11,g12)
    c: Equal(g12,g7)
    c: Radius(g12) = 1
    c: DistanceY(g6,g5) = 2.6
    c: Equal(g6,g0)
    c: Equal(g10,g12)
    c: DistanceY(g-1,g3) = 12
    c: DistanceX(g0,g6) = 25
    c: DistanceX(g2,g4) = 17.2
    c: PointOnObject(g13,g-1)
    c: Horizontal(g13)
    c: Coincident(g14,g6)
    c: PointOnObject(g14,g-1)
    c: Coincident(g15,g14)
    c: Vertical(g15)
    c: Coincident(g16,g15)
    c: Horizontal(g16)
    c: Coincident(g17,g16)
    c: Coincident(g17,g13)
    c: Vertical(g17)
    c: DistanceY(g3,g15) = 10
    c: DistanceX(g6,g14) = 10
    c: Equal(g14,g13)
    c: Coincident(g0,g13)
FEATURE [PartDesign::Pocket] Pocket009  label="SculptAlongZ"
  BaseFeature = -> Pocket008
  Length = 5
  Length2 = 100
  Placement = pos=(0,0,0) rot=(0.57735,0.57735,0.57735;2.0944rad)
  Profile = -> Sketch021
  Reversed = true
  Type = 1
FEATURE [PartDesign::Plane] DatumPlane002  label="Datum_LSRMtCSunk"
  AttachmentOffset = pos=(0,0,-1.2) rot=(0,0,1;0rad)
  Length = 60
  MapMode = 5
  Placement = pos=(0,1.2,3e-16) rot=(1,0,0;1.5708rad)
  ResizeMode = 0
  Support = -> [XZ_Plane001]
  Width = 60
  expr: .AttachmentOffset.Base.z = -1 * <<params>>.lsr_mt_csunk_z
FEATURE [Sketcher::SketchObject] Sketch022  label="Sketch_LSRHoleMt_Temp"
  FullyConstrained = true
  MapMode = 5
  Placement = pos=(0,0,0) rot=(1,0,0;1.5708rad)
  Support = -> [XZ_Plane001]
  expr: Constraints[5] = <<params>>.lsr_mt_hole_spacing_width
  expr: Constraints[4] = <<params>>.lsr_mt_hole_height
  sketch-geometry (2):
    g0: LineSegment StartX=0 StartY=0 StartZ=0 EndX=0 EndY=11 EndZ=0
    g1: LineSegment StartX=-10 StartY=11 StartZ=0 EndX=10 EndY=11 EndZ=0
  constraints (6):
    c: Coincident(g0,g-1)
    c: PointOnObject(g0,g-2)
    c: Horizontal(g1)
    c: Symmetric(g1,g1,g0)
    c: DistanceY(g-1,g0) = 11
    c: DistanceX(g1,g1) = 20
FEATURE [Sketcher::SketchObject] Sketch023  label="Sketch_LSRMtHoles"
  FullyConstrained = true
  MapMode = 5
  Placement = pos=(0,0,0) rot=(1,0,0;1.5708rad)
  Support = -> [XZ_Plane001]
  expr: Constraints[9] = <<params>>.m2_hole_clear_diam
  expr: Constraints[4] = <<params>>.lsr_mt_hole_height
  expr: Constraints[5] = <<params>>.lsr_mt_hole_spacing_width
  sketch-geometry (4):
    g0: LineSegment StartX=0 StartY=0 StartZ=0 EndX=0 EndY=11 EndZ=0
    g1: LineSegment StartX=-10 StartY=11 StartZ=0 EndX=10 EndY=11 EndZ=0
    g2: Circle CenterX=-10 CenterY=11 CenterZ=0 NormalX=0 NormalY=0 NormalZ=1 AngleXU=0 Radius=1.15
    g3: Circle CenterX=10 CenterY=11 CenterZ=0 NormalX=0 NormalY=0 NormalZ=1 AngleXU=0 Radius=1.15
  constraints (10):
    c: Coincident(g0,g-1)
    c: PointOnObject(g0,g-2)
    c: Horizontal(g1)
    c: Symmetric(g1,g1,g0)
    c: DistanceY(g-1,g0) = 11
    c: DistanceX(g1,g1) = 20
    c: Coincident(g2,g1)
    c: Coincident(g3,g1)
    c: Equal(g3,g2)
    c: Diameter(g3) = 2.3
FEATURE [PartDesign::Pocket] Pocket010  label="LSRMtHoles"
  BaseFeature = -> Pocket009
  Length = 5
  Length2 = 100
  Placement = pos=(0,0,0) rot=(0.57735,0.57735,0.57735;2.0944rad)
  Profile = -> Sketch023
  Type = 1
FEATURE [Sketcher::SketchObject] Sketch024  label="Sketch_LSRCSunk"
  FullyConstrained = true
  MapMode = 5
  Placement = pos=(0,1.2,3e-16) rot=(1,0,0;1.5708rad)
  Support = -> [DatumPlane002]
  expr: Constraints[35] = <<params>>.m2_nut_clear_flat
  expr: Constraints[4] = <<params>>.lsr_mt_hole_height
  expr: Constraints[5] = <<params>>.lsr_mt_hole_spacing_width
  sketch-geometry (18):
    g0: LineSegment StartX=0 StartY=0 StartZ=0 EndX=0 EndY=11 EndZ=0
    g1: LineSegment StartX=-10 StartY=11 StartZ=0 EndX=10 EndY=11 EndZ=0
    g2: LineSegment StartX=7.57513 StartY=11 StartZ=0 EndX=8.78756 EndY=8.9 EndZ=0
    g3: LineSegment StartX=8.78756 StartY=8.9 StartZ=0 EndX=11.2124 EndY=8.9 EndZ=0
    g4: LineSegment StartX=11.2124 StartY=13.1 StartZ=0 EndX=8.78756 EndY=13.1 EndZ=0
    g5: LineSegment StartX=8.78756 StartY=13.1 StartZ=0 EndX=7.57513 EndY=11 EndZ=0
    g6: Circle CenterX=10 CenterY=11 CenterZ=0 NormalX=0 NormalY=0 NormalZ=1 AngleXU=0 Radius=2.42487
    g7: LineSegment StartX=-7.57513 StartY=11 StartZ=0 EndX=-8.78756 EndY=13.1 EndZ=0
    g8: LineSegment StartX=-8.78756 StartY=13.1 StartZ=0 EndX=-11.2124 EndY=13.1 EndZ=0
    g9: LineSegment StartX=-11.2124 StartY=8.9 StartZ=0 EndX=-8.78756 EndY=8.9 EndZ=0
    g10: LineSegment StartX=-8.78756 StartY=8.9 StartZ=0 EndX=-7.57513 EndY=11 EndZ=0
    g11: Circle CenterX=-10 CenterY=11 CenterZ=0 NormalX=0 NormalY=0 NormalZ=1 AngleXU=0 Radius=2.42487
    g12: LineSegment StartX=11.2124 StartY=13.1 StartZ=0 EndX=21.2124 EndY=13.1 EndZ=0
    g13: LineSegment StartX=11.2124 StartY=8.9 StartZ=0 EndX=21.2124 EndY=8.9 EndZ=0
    g14: LineSegment StartX=21.2124 StartY=8.9 StartZ=0 EndX=21.2124 EndY=13.1 EndZ=0
    g15: LineSegment StartX=-11.2124 StartY=8.9 StartZ=0 EndX=-21.2124 EndY=8.9 EndZ=0
    g16: LineSegment StartX=-11.2124 StartY=13.1 StartZ=0 EndX=-21.2124 EndY=13.1 EndZ=0
    g17: LineSegment StartX=-21.2124 StartY=8.9 StartZ=0 EndX=-21.2124 EndY=13.1 EndZ=0
  constraints (52):
    c: Coincident(g0,g-1)
    c: PointOnObject(g0,g-2)
    c: Horizontal(g1)
    c: Symmetric(g1,g1,g0)
    c: DistanceY(g-1,g0) = 11
    c: DistanceX(g1,g1) = 20
    c: Coincident(g2,g3)
    c: Coincident(g4,g5)
    c: Coincident(g5,g2)
    c: Equal(g2,g3)
    c: Equal(g2,g4)
    c: Equal(g2,g5)
    c: PointOnObject(g2,g6)
    c: PointOnObject(g3,g6)
    c: PointOnObject(g4,g6)
    c: PointOnObject(g4,g6)
    c: PointOnObject(g5,g6)
    c: Coincident(g6,g1)
    c: Coincident(g7,g8)
    c: Coincident(g9,g10)
    c: Coincident(g10,g7)
    c: Equal(g7,g8)
    c: Equal(g7,g9)
    c: Equal(g7,g10)
    c: PointOnObject(g7,g11)
    c: PointOnObject(g8,g11)
    c: PointOnObject(g9,g11)
    c: PointOnObject(g9,g11)
    c: PointOnObject(g10,g11)
    c: Coincident(g11,g1)
    c: Equal(g11,g6)
    c: PointOnObject(g2,g1)
    c: PointOnObject(g7,g1)
    c: Horizontal(g4)
    c: Horizontal(g8)
    c: DistanceY(g3,g4) = 4.2
    c: Coincident(g12,g4)
    c: Horizontal(g12)
    c: Coincident(g13,g3)
    c: Horizontal(g13)
    c: Coincident(g14,g13)
    c: Coincident(g14,g12)
    c: Vertical(g14)
    c: Coincident(g15,g9)
    c: Coincident(g16,g8)
    c: Horizontal(g16)
    c: Coincident(g17,g15)
    c: Coincident(g17,g16)
    c: Vertical(g17)
    c: Horizontal(g15)
    c: Equal(g12,g16)
    c: Distance(g12) = 10
FEATURE [PartDesign::Pocket] Pocket011  label="LSRMtCSunk"
  BaseFeature = -> Pocket010
  Length = 5
  Length2 = 100
  Placement = pos=(0,0,0) rot=(0.57735,0.57735,0.57735;2.0944rad)
  Profile = -> Sketch024
  Type = 1
FEATURE [Sketcher::SketchObject] Sketch025
  FullyConstrained = true
  MapMode = 5
  Placement = pos=(0,0,0) rot=(1,0,0;1.5708rad)
  Support = -> [XZ_Plane001]
  expr: Constraints[46] = <<params>>.grove_clear_height
  expr: Constraints[50] = <<params>>.grove_clear_width
  expr: Constraints[49] = <<params>>.mt_height
  expr: Constraints[20] = <<params>>.std_rad
  expr: Constraints[48] = <<params>>.std_rad / 4
  expr: Constraints[21] = <<params>>.mt_width
  sketch-geometry (20):
    g0: LineSegment StartX=-12.5 StartY=0 StartZ=0 EndX=-12.5 EndY=13 EndZ=0
    g1: LineSegment StartX=12.5 StartY=13 StartZ=0 EndX=12.5 EndY=0 EndZ=0
    g2: LineSegment StartX=12.5 StartY=0 StartZ=0 EndX=17.5 EndY=0 EndZ=0
    g3: LineSegment StartX=17.5 StartY=0 StartZ=0 EndX=17.5 EndY=20 EndZ=0
    g4: LineSegment StartX=17.5 StartY=20 StartZ=0 EndX=-17.5 EndY=20 EndZ=0
    g5: LineSegment StartX=-17.5 StartY=20 StartZ=0 EndX=-17.5 EndY=0 EndZ=0
    g6: LineSegment StartX=-17.5 StartY=0 StartZ=0 EndX=-12.5 EndY=0 EndZ=0
    g7: ArcOfCircle CenterX=-10.5 CenterY=13 CenterZ=0 NormalX=0 NormalY=0 NormalZ=1 AngleXU=0 Radius=2 StartAngle=1.5708 EndAngle=3.14159
    g8: ArcOfCircle CenterX=10.5 CenterY=13 CenterZ=0 NormalX=0 NormalY=0 NormalZ=1 AngleXU=0 Radius=2 StartAngle=0 EndAngle=1.5708
    g9: LineSegment StartX=-5.75 StartY=13 StartZ=0 EndX=5.75 EndY=13 EndZ=0
    g10: LineSegment StartX=-6.25 StartY=13.5 StartZ=0 EndX=-6.25 EndY=14.5 EndZ=0
    g11: LineSegment StartX=-6.75 StartY=15 StartZ=0 EndX=-10.5 EndY=15 EndZ=0
    g12: LineSegment StartX=6.25 StartY=13.5 StartZ=0 EndX=6.25 EndY=14.5 EndZ=0
    g13: LineSegment StartX=6.75 StartY=15 StartZ=0 EndX=10.5 EndY=15 EndZ=0
    g14: ArcOfCircle CenterX=-6.75 CenterY=14.5 CenterZ=0 NormalX=0 NormalY=0 NormalZ=1 AngleXU=0 Radius=0.5 StartAngle=-9e-16 EndAngle=1.5708
    g15: ArcOfCircle CenterX=-5.75 CenterY=13.5 CenterZ=0 NormalX=0 NormalY=0 NormalZ=1 AngleXU=0 Radius=0.5 StartAngle=3.14159 EndAngle=4.71239
    g16: ArcOfCircle CenterX=5.75 CenterY=13.5 CenterZ=0 NormalX=0 NormalY=0 NormalZ=1 AngleXU=0 Radius=0.5 StartAngle=4.71239 EndAngle=6.28319
    g17: ArcOfCircle CenterX=6.75 CenterY=14.5 CenterZ=0 NormalX=0 NormalY=0 NormalZ=1 AngleXU=0 Radius=0.5 StartAngle=1.5708 EndAngle=3.14159
    g18: LineSegment StartX=0 StartY=0 StartZ=0 EndX=0 EndY=13 EndZ=0
    g19: LineSegment StartX=-6.25 StartY=14.5 StartZ=0 EndX=6.25 EndY=14.5 EndZ=0
  constraints (53):
    c: PointOnObject(g0,g-1)
    c: Vertical(g0)
    c: Vertical(g1)
    c: Coincident(g2,g1)
    c: Horizontal(g2)
    c: Coincident(g3,g2)
    c: Vertical(g3)
    c: Coincident(g4,g3)
    c: Horizontal(g4)
    c: Coincident(g5,g4)
    c: PointOnObject(g5,g-1)
    c: Vertical(g5)
    c: Coincident(g6,g5)
    c: Coincident(g6,g0)
    c: Symmetric(g0,g1,g-1)
    c: Equal(g2,g6)
    c: Distance(g2) = 5
    c: Tangent(g0,g7) = 1.5708
    c: Tangent(g1,g8) = 1.5708
    c: Equal(g8,g7)
    c: Radius(g8) = 2
    c: DistanceX(g0,g1) = 25
    c: Horizontal(g9)
    c: Vertical(g10)
    c: Coincident(g11,g7)
    c: Horizontal(g11)
    c: Vertical(g12)
    c: Coincident(g13,g8)
    c: Horizontal(g13)
    c: Tangent(g11,g14) = -1.5708
    c: Tangent(g10,g14) = -1.5708
    c: Tangent(g10,g15) = 1.5708
    c: Tangent(g9,g15) = -1.5708
    c: Tangent(g9,g16) = -1.5708
    c: Tangent(g12,g16) = -1.5708
    c: Tangent(g12,g17) = 1.5708
    c: Tangent(g13,g17) = 1.5708
    c: Coincident(g18,g-1)
    c: PointOnObject(g18,g-2)
    c: Symmetric(g9,g9,g18)
    c: Equal(g17,g16)
    c: Equal(g16,g15)
    c: Equal(g15,g14)
    c: Coincident(g19,g10)
    c: Coincident(g19,g12)
    c: Horizontal(g19)
    c: DistanceY(g9,g13) = 2
    c: DistanceY(g8,g3) = 5
    c: Radius(g17) = 0.5
    c: DistanceY(g-1,g11) = 15
    c: DistanceX(g10,g12) = 12.5
    c: Tangent(g8,g13)
    c: Tangent(g11,g7)
FEATURE [PartDesign::Pocket] Pocket012  label="SculptLSRPlate"
  BaseFeature = -> Pocket011
  Length = 5
  Length2 = 100
  Placement = pos=(0,0,0) rot=(0.57735,0.57735,0.57735;2.0944rad)
  Profile = -> Sketch025
  Type = 1
FEATURE [PartDesign::Body] Body  label="PB3D_LSRMt"
  Group = -> [Sketch016,Pad010,DatumPlane,DatumPlane001,Sketch017,Sketch018,Pocket006,Sketch019,Pocket007,Sketch020,Pocket008,Sketch021,Pocket009,DatumPlane002,Sketch022,Sketch023,Pocket010,Sketch024,Pocket011,Sketch025,Pocket012]
  Origin = -> Origin001
  Tip = -> Pocket012
FEATURE [Sketcher::SketchObject] Sketch026
  FullyConstrained = true
  MapMode = 5
  Placement = pos=(0,0,0) rot=(1,0,0;1.5708rad)
  Support = -> [XZ_Plane011]
  expr: Constraints[35] = <<params>>.std_rad / 4
  expr: Constraints[36] = <<params>>.grove_clear_height
  expr: Constraints[34] = <<params>>.grove_clear_width
  expr: Constraints[33] = <<params>>.mt_height
  expr: Constraints[32] = <<params>>.std_rad
  expr: Constraints[31] = <<params>>.mt_width
  sketch-geometry (15):
    g0: LineSegment StartX=-12.5 StartY=0 StartZ=0 EndX=12.5 EndY=0 EndZ=0
    g1: LineSegment StartX=12.5 StartY=0 StartZ=0 EndX=12.5 EndY=13 EndZ=0
    g2: LineSegment StartX=-12.5 StartY=13 StartZ=0 EndX=-12.5 EndY=0 EndZ=0
    g3: LineSegment StartX=-10.5 StartY=15 StartZ=0 EndX=-6.75 EndY=15 EndZ=0
    g4: LineSegment StartX=10.5 StartY=15 StartZ=0 EndX=6.75 EndY=15 EndZ=0
    g5: LineSegment StartX=6.25 StartY=14.5 StartZ=0 EndX=6.25 EndY=13.5 EndZ=0
    g6: LineSegment StartX=5.75 StartY=13 StartZ=0 EndX=-5.75 EndY=13 EndZ=0
    g7: LineSegment StartX=-6.25 StartY=13.5 StartZ=0 EndX=-6.25 EndY=14.5 EndZ=0
    g8: ArcOfCircle CenterX=-6.75 CenterY=14.5 CenterZ=0 NormalX=0 NormalY=0 NormalZ=1 AngleXU=0 Radius=0.5 StartAngle=0 EndAngle=1.5708
    g9: ArcOfCircle CenterX=-5.75 CenterY=13.5 CenterZ=0 NormalX=0 NormalY=0 NormalZ=1 AngleXU=0 Radius=0.5 StartAngle=3.14159 EndAngle=4.71239
    g10: ArcOfCircle CenterX=5.75 CenterY=13.5 CenterZ=0 NormalX=0 NormalY=0 NormalZ=1 AngleXU=0 Radius=0.5 StartAngle=4.71239 EndAngle=6.28319
    g11: ArcOfCircle CenterX=6.75 CenterY=14.5 CenterZ=0 NormalX=0 NormalY=0 NormalZ=1 AngleXU=0 Radius=0.5 StartAngle=1.5708 EndAngle=3.14159
    g12: ArcOfCircle CenterX=10.5 CenterY=13 CenterZ=0 NormalX=0 NormalY=0 NormalZ=1 AngleXU=0 Radius=2 StartAngle=0 EndAngle=1.5708
    g13: ArcOfCircle CenterX=-10.5 CenterY=13 CenterZ=0 NormalX=0 NormalY=0 NormalZ=1 AngleXU=0 Radius=2 StartAngle=1.5708 EndAngle=3.14159
    g14: LineSegment StartX=-6.25 StartY=14.5 StartZ=0 EndX=6.25 EndY=14.5 EndZ=0
  constraints (37):
    c: Coincident(g0,g1)
    c: Coincident(g2,g0)
    c: Horizontal(g0)
    c: Vertical(g1)
    c: Vertical(g2)
    c: Symmetric(g0,g0,g-1)
    c: Horizontal(g3)
    c: Horizontal(g4)
    c: Vertical(g5)
    c: Horizontal(g6)
    c: Vertical(g7)
    c: Tangent(g3,g8) = 1.5708
    c: Tangent(g7,g8) = -1.5708
    c: Tangent(g6,g9) = 1.5708
    c: Tangent(g7,g9) = 1.5708
    c: Tangent(g6,g10) = 1.5708
    c: Tangent(g5,g10) = 1.5708
    c: Tangent(g4,g11) = -1.5708
    c: Tangent(g5,g11) = -1.5708
    c: Tangent(g4,g12) = -1.5708
    c: Tangent(g1,g12) = -1.5708
    c: Tangent(g3,g13) = 1.5708
    c: Tangent(g2,g13) = -1.5708
    c: Equal(g11,g10)
    c: Equal(g10,g9)
    c: Equal(g9,g8)
    c: Equal(g13,g12)
    c: Coincident(g14,g7)
    c: Coincident(g14,g5)
    c: Horizontal(g14)
    c: Equal(g4,g3)
    c: DistanceX(g0,g0) = 25
    c: Radius(g12) = 2
    c: DistanceY(g0,g4) = 15
    c: DistanceX(g7,g5) = 12.5
    c: Radius(g11) = 0.5
    c: DistanceY(g6,g4) = 2
FEATURE [PartDesign::Pad] Pad011  label="MainExt001"
  Direction = (1,1,1)
  Length = 1.6
  Length2 = 100
  Placement = pos=(0,0,0) rot=(1,0,0;1.5708rad)
  Profile = -> Sketch026
  Type = 0
  expr: Length = <<params>>.faceplate_thick
FEATURE [Sketcher::SketchObject] Sketch027  label="Sketch_LSRMtHoles001"
  FullyConstrained = true
  MapMode = 5
  Placement = pos=(0,0,0) rot=(1,0,0;1.5708rad)
  Support = -> [XZ_Plane011]
  expr: Constraints[5] = <<params>>.lsr_mt_hole_spacing_width
  expr: Constraints[4] = <<params>>.lsr_mt_hole_height
  expr: Constraints[9] = <<params>>.m2_hole_clear_diam
  sketch-geometry (4):
    g0: LineSegment StartX=0 StartY=0 StartZ=0 EndX=0 EndY=11 EndZ=0
    g1: LineSegment StartX=-10 StartY=11 StartZ=0 EndX=10 EndY=11 EndZ=0
    g2: Circle CenterX=-10 CenterY=11 CenterZ=0 NormalX=0 NormalY=0 NormalZ=1 AngleXU=0 Radius=1.15
    g3: Circle CenterX=10 CenterY=11 CenterZ=0 NormalX=0 NormalY=0 NormalZ=1 AngleXU=0 Radius=1.15
  constraints (10):
    c: Coincident(g0,g-1)
    c: PointOnObject(g0,g-2)
    c: Horizontal(g1)
    c: Symmetric(g1,g1,g0)
    c: DistanceY(g-1,g0) = 11
    c: DistanceX(g1,g1) = 20
    c: Coincident(g2,g1)
    c: Coincident(g3,g1)
    c: Equal(g3,g2)
    c: Diameter(g3) = 2.3
FEATURE [PartDesign::Pocket] Pocket013  label="LSRMtHoles001"
  BaseFeature = -> Pad011
  Length = 5
  Length2 = 100
  Placement = pos=(0,0,0) rot=(1,0,0;1.5708rad)
  Profile = -> Sketch027
  Reversed = true
  Type = 1
FEATURE [Sketcher::SketchObject] Sketch028
  FullyConstrained = true
  MapMode = 5
  Placement = pos=(0,0,0) rot=(1,0,0;1.5708rad)
  Support = -> [XZ_Plane011]
  expr: Constraints[34] = <<params>>.mt_height
  expr: Constraints[33] = <<params>>.faceplate_cut_width
  expr: Constraints[32] = <<params>>.mt_width
  expr: Constraints[30] = <<params>>.std_rad / 2
  expr: Constraints[12] = <<params>>.faceplate_bottom_height
  expr: Constraints[11] = <<params>>.std_rad / 2
  sketch-geometry (14):
    g0: LineSegment StartX=7.9 StartY=14 StartZ=0 EndX=7.9 EndY=3 EndZ=0
    g1: LineSegment StartX=6.9 StartY=2 StartZ=0 EndX=-6.9 EndY=2 EndZ=0
    g2: LineSegment StartX=-7.9 StartY=3 StartZ=0 EndX=-7.9 EndY=14 EndZ=0
    g3: LineSegment StartX=0 StartY=0 StartZ=0 EndX=0 EndY=2 EndZ=0
    g4: ArcOfCircle CenterX=-6.9 CenterY=3 CenterZ=0 NormalX=0 NormalY=0 NormalZ=1 AngleXU=0 Radius=1 StartAngle=3.14159 EndAngle=4.71239
    g5: ArcOfCircle CenterX=6.9 CenterY=3 CenterZ=0 NormalX=0 NormalY=0 NormalZ=1 AngleXU=0 Radius=1 StartAngle=4.71239 EndAngle=6.28319
    g6: LineSegment StartX=8.9 StartY=15 StartZ=0 EndX=12.5 EndY=15 EndZ=0
    g7: LineSegment StartX=-8.9 StartY=15 StartZ=0 EndX=-12.5 EndY=15 EndZ=0
    g8: LineSegment StartX=-12.5 StartY=15 StartZ=0 EndX=-12.5 EndY=17 EndZ=0
    g9: LineSegment StartX=-12.5 StartY=17 StartZ=0 EndX=12.5 EndY=17 EndZ=0
    g10: LineSegment StartX=12.5 StartY=17 StartZ=0 EndX=12.5 EndY=15 EndZ=0
    g11: ArcOfCircle CenterX=-8.9 CenterY=14 CenterZ=0 NormalX=0 NormalY=0 NormalZ=1 AngleXU=0 Radius=1 StartAngle=6e-16 EndAngle=1.5708
    g12: ArcOfCircle CenterX=8.9 CenterY=14 CenterZ=0 NormalX=0 NormalY=0 NormalZ=1 AngleXU=0 Radius=1 StartAngle=1.5708 EndAngle=3.14159
    g13: LineSegment StartX=-7.9 StartY=14 StartZ=0 EndX=7.9 EndY=14 EndZ=0
  constraints (36):
    c: Horizontal(g1)
    c: Vertical(g0)
    c: Vertical(g2)
    c: Coincident(g3,g-1)
    c: PointOnObject(g3,g-2)
    c: Tangent(g2,g4) = 1.5708
    c: Tangent(g1,g4) = 1.5708
    c: Tangent(g1,g5) = 1.5708
    c: Tangent(g0,g5) = 1.5708
    c: Symmetric(g1,g1,g3)
    c: Equal(g5,g4)
    c: Radius(g5) = 1
    c: DistanceY(g-1,g3) = 2
    c: Horizontal(g6)
    c: Horizontal(g7)
    c: Coincident(g8,g7)
    c: Vertical(g8)
    c: Coincident(g9,g8)
    c: Horizontal(g9)
    c: Coincident(g10,g9)
    c: Coincident(g10,g6)
    c: Vertical(g10)
    c: Tangent(g2,g11) = -1.5708
    c: Tangent(g7,g11) = -1.5708
    c: Tangent(g0,g12) = -1.5708
    c: Tangent(g6,g12) = 1.5708
    c: Coincident(g13,g2)
    c: Coincident(g13,g0)
    c: Horizontal(g13)
    c: Equal(g6,g7)
    c: Radius(g12) = 1
    c: Equal(g12,g11)
    c: DistanceX(g8,g9) = 25
    c: DistanceX(g2,g0) = 15.8
    c: DistanceY(g-1,g6) = 15
    c: Distance(g10) = 2
FEATURE [PartDesign::Pocket] Pocket014  label="ElectronicsClear"
  BaseFeature = -> Pocket013
  Length = 5
  Length2 = 100
  Placement = pos=(0,0,0) rot=(1,0,0;1.5708rad)
  Profile = -> Sketch028
  Reversed = true
  Type = 1
FEATURE [PartDesign::Body] Body008  label="PB3D_LSRMt_FacePlate"
  Group = -> [Sketch026,Pad011,Sketch027,Pocket013,Sketch028,Pocket014]
  Origin = -> Origin010
  Tip = -> Pocket014
FEATURE [App::Part] Part  label="PB3D_LSR_Mt_Part"
  Group = -> [Body,Body008]
  Origin = -> Origin
FEATURE [Mesh::Feature] Mesh  label="PB3D_LSRMt (Meshed)"
FEATURE [Mesh::Feature] Mesh001  label="PB3D_LSRMt_FacePlate (Meshed)"
